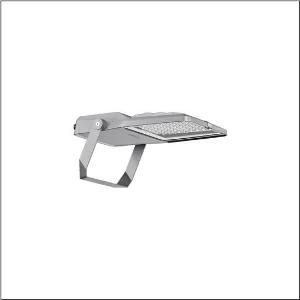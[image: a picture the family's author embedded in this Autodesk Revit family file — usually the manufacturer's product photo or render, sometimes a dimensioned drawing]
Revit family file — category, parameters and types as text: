
# Revit family: floodlight_fl_21_iq_mini___rs12_5xa7772b3b1a_fd5e
name_source: partatom
category: Lighting Fixtures
units: mm (PartAtom-declared; Revit-internal decimal feet)

## family parameters
Cut with Voids When Loaded = No
Host = Face
Light Source = No
Part Type = Normal
Room Calculation Point = No
Round Connector Dimension = Use Diameter
Shared = No

## types (1)
- --- (1 x LED, 5430 lm, 45.5 W, 3000K)
    Apparent Load = 46 VA
    CIE Flux Codes = 79 92 99 100 100
    Color Rendering = 80
    Color Temperature = 3000K
    Default Elevation = 1800 mm
    Description = Floodlight FL 21 iQ mini, floodlight, primary light control with lens, of PMMA, primary optical cover: protective disc, of toughened safety glass, transparent, light distribution: RS12, light emission: direct distribution, installation type: surface-mounted, LED, High Power LED, rated luminous flux: 5.430lm, luminous efficacy: 119lm/W, light colour: 830, colour temperature: 3000K, control: Street-Remote, Auto-Match, Temp-Guard, Night-Set, Smart-Wire, Desk-Remote (wireless, voltage-free reading and setting of iQ features in the workshop via application-optimized NFC function/RFID function), optimised constant luminous flux control (CLO 2.0), with terminal, 6-pole, mains connection: 220..240V, AC, 50/60Hz, start of lifetime: 46W, end of service life: 48W, reduction: 21W, luminaire housing, of diecast aluminium, powder-coated, Siteco® metallic grey (DB 702S), corrosivity category C5 mid according to DIN EN ISO 12944, sealing non-destructively replaceable, mounting bracket, of steel, galvanised, powder-coated, Siteco® metallic grey (DB 702S), protection rating (complete): IP66, insulation class (complete): insulation class II (safety insulation), certification: CE, ENEC, VDE, protection symbol: D, impact resistance: IK08, permissible operating ambient temperature: -40..+40°C, permissible operating ambient temperature for outdoor applications: -40..+50°C, standard: DIN EN 12944, LABS conformity tested according to VDMA 24364:2018-05, packaging unit: 1 piece

Light Distribution: RS12
    Height = 70 mm
    Lamp = 1 x LED
    Lamp Light Flux = 5430 lm
    Lamp Power = 45.5 W
    Lamp count = 1
    Length = 485 mm
    Luminous efficacy = 119 lm/W
    Manufacturer = Siteco
    ModVariant = No
    Model = 5XA7772B3B1A
    Number of Poles = 1
    OnlyDefault = Yes
    Power Factor = 1
    Product Name = Floodlight FL 21 iQ mini | RS12
    Product group = floodlight | pylon annexe
    ProductGroupID = 6200
    Protection Class = Protection class II
    Protection Degree = IP 66
    RLX_Detail_Level = 1
    RLX_Emergency_Light_Flux = 0 lm
    RLX_Emergency_Type = 0
    RLX_Emergency_Type_DB = No
    RlxData = <blob elided: 90989 chars, md5=6f86b17d>
    Socket = socket
    Standby Power = 0 W
    System Light Flux = 5430 lm
    System Power = 46 W
    Type Comments = factory setting: luminous flux: 100 % | dim-lin: 254 | 463 mA
    Type Image = l_1006845.jpg
    URL = http://relux.com
    VarID = @adj_100167
    Voltage = 0 V
    Weight = 0.00 kg
    Width = 337 mm

## geometry (parser evidence)
native form markers: Blend x4, Sweep x11
no freeform markers — native parametric forms only
